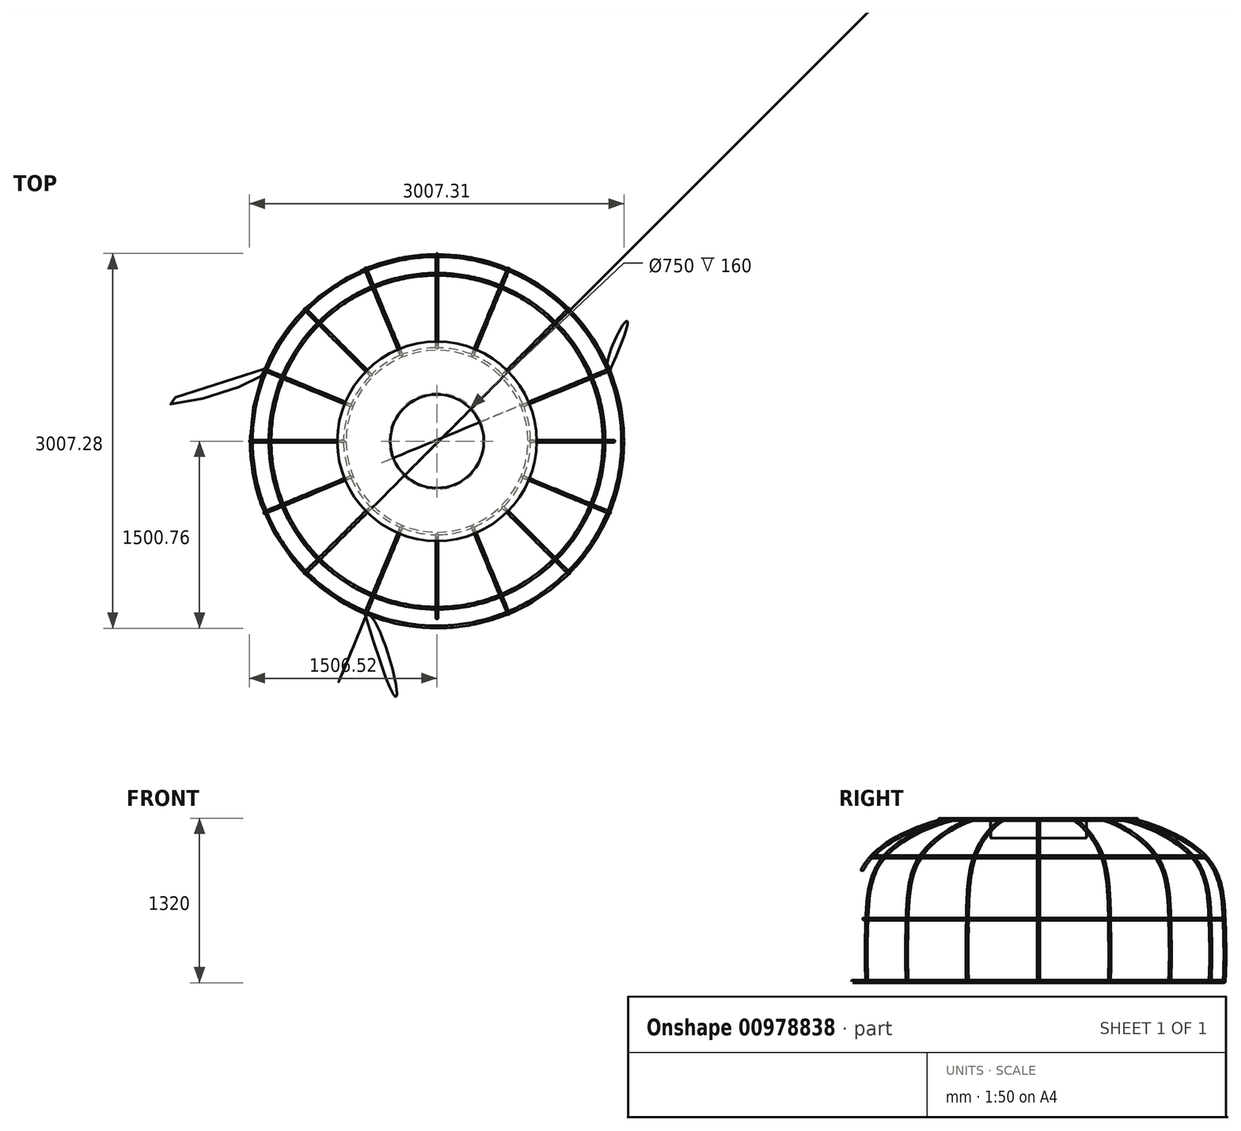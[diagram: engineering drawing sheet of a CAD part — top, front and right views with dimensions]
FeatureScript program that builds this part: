
annotation { "Feature Type Name" : "Feature", "Feature Type Description" : "" }
export const myFeature = defineFeature(function(context is Context, id is Id, definition is map)
    precondition{}
    {
        {
            var Q0;
            Q0=qCreatedBy(makeId("Top.planeOp"),FACE);
            var sketch = newSketch(context, id + "F0", { "sketchPlane" : qUnion([Q0])});
            skCircle(sketch, "E0", {"center": v(0, 0) * mm, "radius": 1490 * mm});
            skSolve(sketch);
        }
        {
            var Q0;
            Q0=qCreatedBy(makeId("Top.planeOp"),FACE);
            cPlane(context, id + "F1", {"entities" : qUnion([Q0]), "cplaneType" : CPlaneType.OFFSET, "offset" : 500 * mm, "width" : 150 * mm, "height" : 150 * mm});
        }
        {
            var Q0;
            Q0=qCreatedBy(id+"F1.planeOp",FACE);
            var sketch = newSketch(context, id + "F2", { "sketchPlane" : qUnion([Q0])});
            skCircle(sketch, "E1", {"center": v(0, 0) * mm, "radius": 1490 * mm});
            skSolve(sketch);
        }
        {
            var Q0;
            Q0=qCreatedBy(id+"F1.planeOp",FACE);
            cPlane(context, id + "F3", {"entities" : qUnion([Q0]), "cplaneType" : CPlaneType.OFFSET, "offset" : 500 * mm, "width" : 150 * mm, "height" : 150 * mm});
        }
        {
            var Q0;
            Q0=qCreatedBy(id+"F3.planeOp",FACE);
            var sketch = newSketch(context, id + "F4", { "sketchPlane" : qUnion([Q0])});
            skCircle(sketch, "E2", {"center": v(0, 0) * mm, "radius": 1340 * mm});
            skSolve(sketch);
        }
        {
            var Q0;
            Q0=qCreatedBy(id+"F3.planeOp",FACE);
            cPlane(context, id + "F5", {"entities" : qUnion([Q0]), "cplaneType" : CPlaneType.OFFSET, "offset" : 300 * mm, "width" : 150 * mm, "height" : 150 * mm});
        }
        {
            var Q0;
            Q0=qCreatedBy(id+"F5.planeOp",FACE);
            var sketch = newSketch(context, id + "F6", { "sketchPlane" : qUnion([Q0])});
            skCircle(sketch, "E3", {"center": v(0, 0) * mm, "radius": 740 * mm});
            skSolve(sketch);
        }
        {
            var Q0;
            Q0=qCreatedBy(makeId("Right.planeOp"),FACE);
            var sketch = newSketch(context, id + "F7", { "sketchPlane" : qUnion([Q0])});
            skCircle(sketch, "E4", {"center": v(1490, 0) * mm, "radius": 10 * mm});
            skSolve(sketch);
        }
        {
            var Q0;
            Q0=makeQuery(id+"F7.imprint","IMPRINT",FACE,{"disambiguationData":[TD([[makeQuery(id+"F7.imprint","IMPRINT",EDGE,{"derivedFrom":sQuery(id+"F7.wireOp",EDGE,"E4")}),1.0]])]});
            var Q1;
            Q1=sQuery(id+"F0.wireOp",EDGE,"E0");
            sweep(context, id + "F8", {"profiles" : qUnion([Q0]), "path" : qUnion([Q1])});
        }
        {
            var Q0;
            Q0=qCreatedBy(makeId("Right.planeOp"),FACE);
            var sketch = newSketch(context, id + "F9", { "sketchPlane" : qUnion([Q0])});
            skCircle(sketch, "E5", {"center": v(1490, 500) * mm, "radius": 10 * mm});
            skSolve(sketch);
        }
        {
            var Q0;
            Q0=makeQuery(id+"F9.imprint","IMPRINT",FACE,{"disambiguationData":[TD([[makeQuery(id+"F9.imprint","IMPRINT",EDGE,{"derivedFrom":sQuery(id+"F9.wireOp",EDGE,"E5")}),1.0]])]});
            var Q1;
            Q1=sQuery(id+"F2.wireOp",EDGE,"E1");
            sweep(context, id + "F10", {"profiles" : qUnion([Q0]), "path" : qUnion([Q1])});
        }
        {
            var Q0;
            Q0=qCreatedBy(makeId("Right.planeOp"),FACE);
            var sketch = newSketch(context, id + "F11", { "sketchPlane" : qUnion([Q0])});
            skCircle(sketch, "E6", {"center": v(1340, 1000) * mm, "radius": 10 * mm});
            skSolve(sketch);
        }
        {
            var Q0;
            Q0=makeQuery(id+"F11.imprint","IMPRINT",FACE,{"disambiguationData":[TD([[makeQuery(id+"F11.imprint","IMPRINT",EDGE,{"derivedFrom":sQuery(id+"F11.wireOp",EDGE,"E6")}),1.0]])]});
            var Q1;
            Q1=sQuery(id+"F4.wireOp",EDGE,"E2");
            sweep(context, id + "F12", {"profiles" : qUnion([Q0]), "path" : qUnion([Q1])});
        }
        {
            var Q0;
            Q0=qCreatedBy(makeId("Right.planeOp"),FACE);
            var sketch = newSketch(context, id + "F13", { "sketchPlane" : qUnion([Q0])});
            skCircle(sketch, "E7", {"center": v(740, 1300) * mm, "radius": 10 * mm});
            skSolve(sketch);
        }
        {
            var Q0;
            Q0=makeQuery(id+"F13.imprint","IMPRINT",FACE,{"disambiguationData":[TD([[makeQuery(id+"F13.imprint","IMPRINT",EDGE,{"derivedFrom":sQuery(id+"F13.wireOp",EDGE,"E7")}),1.0]])]});
            var Q1;
            Q1=sQuery(id+"F6.wireOp",EDGE,"E3");
            sweep(context, id + "F14", {"profiles" : qUnion([Q0]), "path" : qUnion([Q1])});
        }
        {
            var Q0;
            Q0=qCreatedBy(id+"F5.planeOp",FACE);
            var sketch = newSketch(context, id + "F15", { "sketchPlane" : qUnion([Q0])});
            skCircle(sketch, "E8", {"center": v(0, 0) * mm, "radius": 800 * mm});
            skCircle(sketch, "E9", {"center": v(0, 0) * mm, "radius": 375 * mm});
            skSolve(sketch);
        }
        {
            var Q0;
            Q0=makeQuery(id+"F15.imprint","IMPRINT",FACE,{"disambiguationData":[TD([[makeQuery(id+"F15.imprint","IMPRINT",EDGE,{"derivedFrom":sQuery(id+"F15.wireOp",EDGE,"E8")}),1.0]])]});
            extrude(context, id + "F16", {"entities" : qUnion([Q0]), "operationType" : NewBodyOperationType.ADD, "depth" : 10 * mm, "offsetDistance" : 25 * mm});
        }
        {
            var Q0;
            Q0=qCreatedBy(makeId("Right.planeOp"),FACE);
            var sketch = newSketch(context, id + "F17", { "sketchPlane" : qUnion([Q0])});
            skLineSegment(sketch, "E10.bottom", {"start": v(375, 1300) * mm, "end": v(385, 1300) * mm});
            skLineSegment(sketch, "E10.top", {"start": v(375, 1150) * mm, "end": v(385, 1150) * mm});
            skLineSegment(sketch, "E10.left", {"start": v(375, 1300) * mm, "end": v(375, 1150) * mm});
            skLineSegment(sketch, "E10.right", {"start": v(385, 1300) * mm, "end": v(385, 1150) * mm});
            skSolve(sketch);
        }
        {
            var Q0;
            Q0=makeQuery(id+"F17.imprint","IMPRINT",FACE,{"disambiguationData":[TD([[makeQuery(id+"F17.imprint","IMPRINT",EDGE,{"derivedFrom":sQuery(id+"F17.wireOp",EDGE,"E10.bottom")}),-1.0]])]});
            var Q1;
            Q1=makeQuery(id+"F16.opExtrude","CAP_EDGE",EDGE,{"disambiguationData":[OSD([sQuery(id+"F15.wireOp",EDGE,"E9")])],"isStart":true});
            sweep(context, id + "F18", {"operationType" : NewBodyOperationType.ADD, "profiles" : qUnion([Q0]), "path" : qUnion([Q1])});
        }
        {
            var Q0;
            Q0=qCreatedBy(makeId("Right.planeOp"),FACE);
            var sketch = newSketch(context, id + "F19", { "sketchPlane" : qUnion([Q0])});
            skFitSpline(sketch, "E11", {"points": [v(1490, 0) * mm, v(1490, 500) * mm, v(1340, 1000) * mm, v(740, 1300) * mm], "startDerivative": vector(92.63, 1197) * mm, "endDerivative": vector(-1335.07, 255.6) * mm});
            skSolve(sketch);
        }
        {
            var Q0;
            Q0=qCreatedBy(makeId("Top.planeOp"),FACE);
            var sketch = newSketch(context, id + "F20", { "sketchPlane" : qUnion([Q0])});
            skCircle(sketch, "E12", {"center": v(0, 1490) * mm, "radius": 10 * mm});
            skSolve(sketch);
        }
        {
            var Q0;
            Q0 = qSketchRegion(id + "F20", true);
            var Q1;
            Q1 = qConstructionFilter(qBodyType(qCreatedBy(id + "F19" ,EDGE), BodyType.WIRE), ConstructionObject.NO);
            sweep(context, id + "F21", {"profiles" : qUnion([Q0]), "path" : qUnion([Q1])});
        }
        {
            var Q0;
            Q0=makeQuery(id+"F21.opSweep","SWEPT_BODY",BODY,{"disambiguationData":[OSD([sQuery(id+"F19.wireOp",EDGE,"E11"),sQuery(id+"F20.wireOp",EDGE,"E12")])]});
            var Q1;
            Q1=makeQuery(id+"F18.opSweep","SWEPT_FACE",FACE,{"disambiguationData":[OSD([sQuery(id+"F15.wireOp",EDGE,"E9"),sQuery(id+"F17.wireOp",EDGE,"E10.left")])]});
            circularPattern(context, id + "F22", {"operationType" : NewBodyOperationType.ADD, "entities" : qUnion([Q0]), "axis" : qUnion([Q1]), "angle" : 360 * degree, "instanceCount" : 16, "equalSpace" : true});
        }
        {
            var Q0;
            Q0=qCreatedBy(makeId("Front.planeOp"),FACE);
            var sketch = newSketch(context, id + "F23", { "sketchPlane" : qUnion([Q0])});
            skLineSegment(sketch, "E13", {"start": v(-562.08, 461.9) * mm, "end": v(-562.08, 437.96) * mm});
            skLineSegment(sketch, "E14", {"start": v(-562.08, 437.96) * mm, "end": v(-10.18, 10.26) * mm});
            skLineSegment(sketch, "E15", {"start": v(-10.18, 10.26) * mm, "end": v(10.53, 10.26) * mm});
            skLineSegment(sketch, "E16", {"start": v(10.53, 10.26) * mm, "end": v(563.96, 439.86) * mm});
            skLineSegment(sketch, "E17", {"start": v(563.96, 439.86) * mm, "end": v(562.9, 460.05) * mm});
            skLineSegment(sketch, "E18", {"start": v(562.9, 460.05) * mm, "end": v(10.53, 889.49) * mm});
            skLineSegment(sketch, "E19", {"start": v(10.53, 889.49) * mm, "end": v(-10.54, 889.49) * mm});
            skLineSegment(sketch, "E20", {"start": v(-10.54, 889.49) * mm, "end": v(-562.08, 461.9) * mm});
            skSolve(sketch);
        }
        {
            var Q0;
            Q0 = qSketchRegion(id + "F23", true);
            extrude(context, id + "F24", {"entities" : qUnion([Q0]), "operationType" : NewBodyOperationType.REMOVE, "endBound" : BoundingType.THROUGH_ALL, "depth" : 25 * mm, "offsetDistance" : 25 * mm});
        }
        {
            var Q0;
            Q0=qCreatedBy(makeId("Right.planeOp"),FACE);
            var sketch = newSketch(context, id + "F25", { "sketchPlane" : qUnion([Q0])});
            skLineSegment(sketch, "E21", {"start": v(-562.2, 462.77) * mm, "end": v(-562.2, 437.36) * mm});
            skLineSegment(sketch, "E22", {"start": v(-562.2, 437.36) * mm, "end": v(-11.46, 10.7) * mm});
            skLineSegment(sketch, "E23", {"start": v(-11.46, 10.7) * mm, "end": v(11.58, 10.7) * mm});
            skLineSegment(sketch, "E24", {"start": v(11.58, 10.7) * mm, "end": v(562.89, 439.18) * mm});
            skLineSegment(sketch, "E25", {"start": v(562.89, 439.18) * mm, "end": v(561.5, 460.98) * mm});
            skLineSegment(sketch, "E26", {"start": v(561.5, 460.98) * mm, "end": v(11.58, 888.9) * mm});
            skLineSegment(sketch, "E27", {"start": v(11.58, 888.9) * mm, "end": v(-11.52, 888.9) * mm});
            skLineSegment(sketch, "E28", {"start": v(-11.52, 888.9) * mm, "end": v(-562.2, 462.77) * mm});
            skSolve(sketch);
        }
        {
            var Q0;
            Q0 = qSketchRegion(id + "F25", true);
            extrude(context, id + "F26", {"entities" : qUnion([Q0]), "operationType" : NewBodyOperationType.REMOVE, "endBound" : BoundingType.THROUGH_ALL, "depth" : 25 * mm, "offsetDistance" : 25 * mm});
        }
    });
